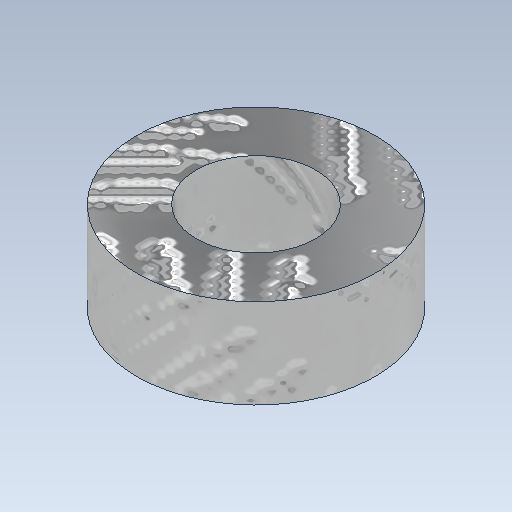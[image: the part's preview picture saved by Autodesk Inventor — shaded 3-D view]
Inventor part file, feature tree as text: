
AUTODESK INVENTOR PART (.ipt)
format: ipt  version: 2020.3 (Build 243373000, 373)  size: 165,888 bytes
history: native  units: mm
features: other x1, extrude x1, sketch x1
ambient origin geometry x8: Origin, YZ Plane, XZ Plane, XY Plane, X Axis, Y Axis, Z Axis, Center Point
bodies: Body1 (feature_tree)
feature tree (3):
  other  "ソリッド1"
  extrude  "押し出し1"  Depth=8.0mm
  sketch  "スケッチ1"
